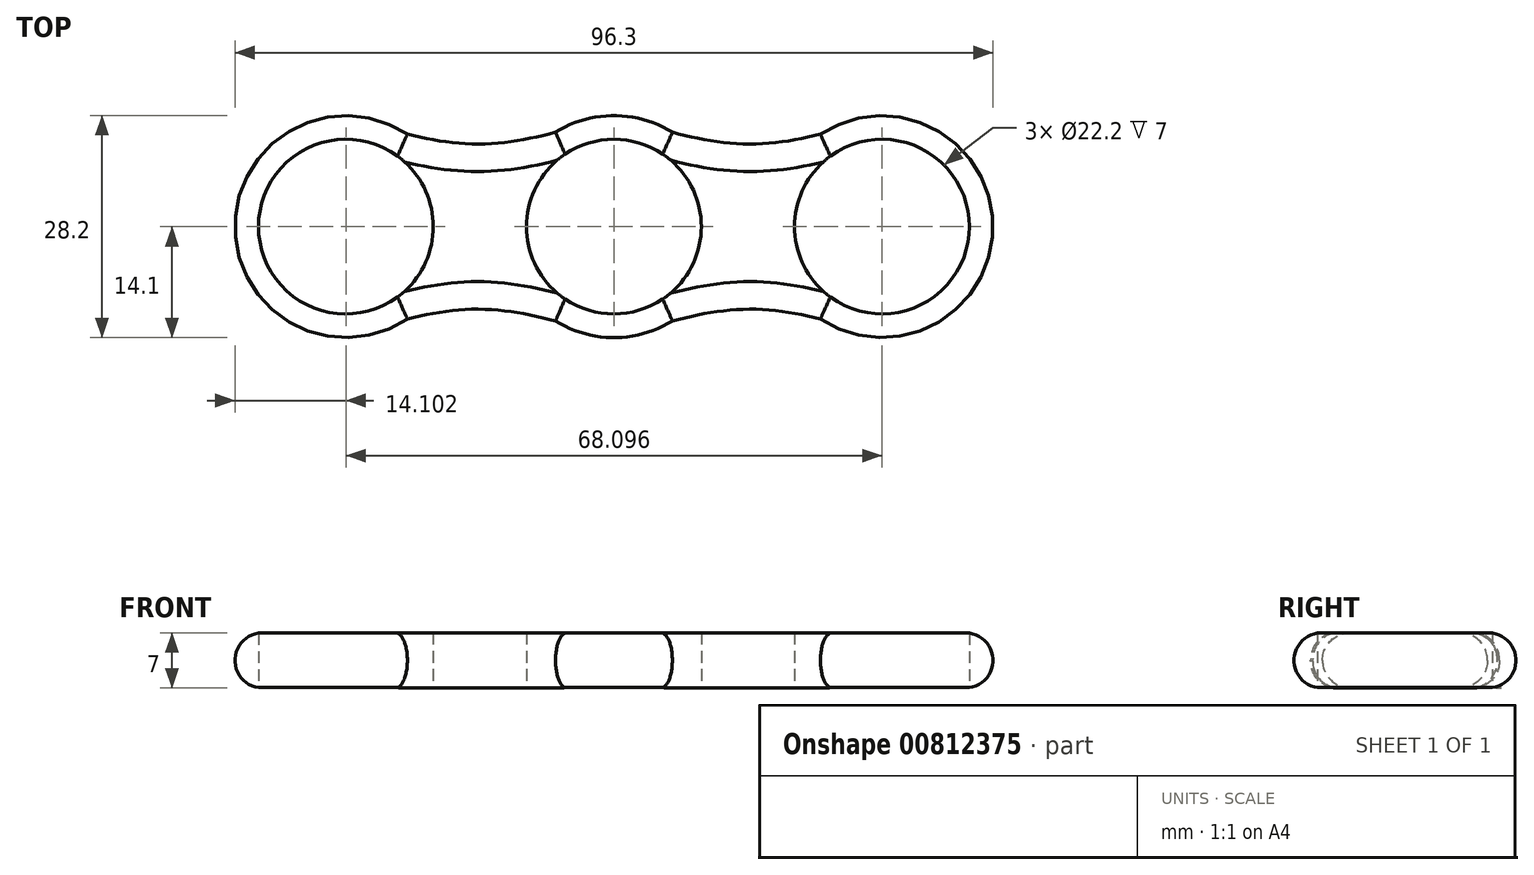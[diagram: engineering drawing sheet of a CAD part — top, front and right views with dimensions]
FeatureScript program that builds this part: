
annotation { "Feature Type Name" : "Feature", "Feature Type Description" : "" }
export const myFeature = defineFeature(function(context is Context, id is Id, definition is map)
    precondition{}
    {
        {
            var Q0;
            Q0=qCreatedBy(makeId("Top.planeOp"),FACE);
            var sketch = newSketch(context, id + "F0", { "sketchPlane" : qUnion([Q0])});
            skCircle(sketch, "E0", {"center": v(0, 0) * mm, "radius": 11.1 * mm});
            skCircle(sketch, "E1", {"center": v(0, 0) * mm, "radius": 14.1 * mm});
            skLineSegment(sketch, "E2", {"start": v(0, 0) * mm, "end": v(45, 0) * mm, "construction": true});
            skCircle(sketch, "E3", {"center": v(34.05, 0) * mm, "radius": 11.1 * mm});
            skCircle(sketch, "E4", {"center": v(34.05, 0) * mm, "radius": 14.1 * mm});
            skLineSegment(sketch, "E5", {"start": v(34.05, -14.1) * mm, "end": v(34.05, 14.1) * mm});
            skFitSpline(sketch, "E6", {"points": [v(34.05, 14.1) * mm, v(0, 14.1) * mm], "startDerivative": vector(-47.35, -16.05) * mm, "endDerivative": vector(-43.28, 12.76) * mm});
            skFitSpline(sketch, "E7.MirrorCS", {"points": [v(34.05, -14.1) * mm, v(0, -14.1) * mm], "startDerivative": vector(-47.35, 16.05) * mm, "endDerivative": vector(-43.28, -12.76) * mm});
            skLineSegment(sketch, "E8", {"start": v(0, -14.1) * mm, "end": v(0, 14.1) * mm, "construction": true});
            skFitSpline(sketch, "E9.MirrorCS", {"points": [v(-34.05, 14.1) * mm, v(0, 14.1) * mm], "startDerivative": vector(47.35, -16.05) * mm, "endDerivative": vector(43.28, 12.76) * mm});
            skCircle(sketch, "E10.MirrorC", {"center": v(-34.05, 0) * mm, "radius": 11.1 * mm});
            skCircle(sketch, "E11.MirrorC", {"center": v(-34.05, 0) * mm, "radius": 14.1 * mm});
            skFitSpline(sketch, "E12.MirrorCS", {"points": [v(-34.05, -14.1) * mm, v(0, -14.1) * mm], "startDerivative": vector(47.35, 16.05) * mm, "endDerivative": vector(43.28, -12.76) * mm});
            skSolve(sketch);
        }
        {
            var Q0;
            Q0 = qSketchRegion(id + "F0", true);
            extrude(context, id + "F1", {"entities" : qUnion([Q0]), "depth" : 7 * mm, "offsetDistance" : 25 * mm});
        }
        {
            var Q0;
            Q0=makeQuery(id+"F1.opExtrude","CAP_EDGE",EDGE,{"disambiguationData":[OSD([sQuery(id+"F0.wireOp",EDGE,"E9.MirrorCS")])],"isStart":false});
            var Q1;
            Q1=makeQuery(id+"F1.opExtrude","CAP_EDGE",EDGE,{"disambiguationData":[OSD([sQuery(id+"F0.wireOp",EDGE,"E11.MirrorC")])],"isStart":false});
            var Q2;
            Q2=makeQuery(id+"F1.opExtrude","CAP_EDGE",EDGE,{"disambiguationData":[OSD([sQuery(id+"F0.wireOp",EDGE,"E12.MirrorCS")])],"isStart":false});
            var Q3;
            {var subQ0=sQuery(id+"F0.wireOp",EDGE,"E12.MirrorCS");var subQ1=sQuery(id+"F0.wireOp",EDGE,"E7.MirrorCS");var subQ2=sQuery(id+"F0.wireOp",EDGE,"E1");Q3=makeQuery(id+"F1.opExtrude","CAP_EDGE",EDGE,{"disambiguationData":[OSD([subQ2]),TDD([makeQuery(id+"F0.imprint","IMPRINT",EDGE,{"disambiguationData":[TD([[makeQuery(id+"F0.imprint","INTERSECT",VERTEX,{"derivedFrom":[subQ2,subQ0]}),-1.0]])],"derivedFrom":subQ2}),makeQuery(id+"F0.imprint","IMPRINT",EDGE,{"disambiguationData":[TD([[makeQuery(id+"F0.imprint","INTERSECT",VERTEX,{"derivedFrom":[subQ2,subQ1]}),1.0]])],"derivedFrom":subQ2})])],"isStart":false});}
            var Q4;
            Q4=makeQuery(id+"F1.opExtrude","CAP_EDGE",EDGE,{"disambiguationData":[OSD([sQuery(id+"F0.wireOp",EDGE,"E7.MirrorCS")])],"isStart":false});
            var Q5;
            {var subQ0=sQuery(id+"F0.wireOp",EDGE,"E9.MirrorCS");var subQ1=sQuery(id+"F0.wireOp",EDGE,"E6");var subQ2=sQuery(id+"F0.wireOp",EDGE,"E1");Q5=makeQuery(id+"F1.opExtrude","CAP_EDGE",EDGE,{"disambiguationData":[OSD([subQ2]),TDD([makeQuery(id+"F0.imprint","IMPRINT",EDGE,{"disambiguationData":[TD([[makeQuery(id+"F0.imprint","INTERSECT",VERTEX,{"derivedFrom":[subQ2,subQ1]}),-1.0]])],"derivedFrom":subQ2}),makeQuery(id+"F0.imprint","IMPRINT",EDGE,{"disambiguationData":[TD([[makeQuery(id+"F0.imprint","INTERSECT",VERTEX,{"derivedFrom":[subQ2,subQ0]}),1.0]])],"derivedFrom":subQ2})])],"isStart":false});}
            var Q6;
            Q6=makeQuery(id+"F1.opExtrude","CAP_EDGE",EDGE,{"disambiguationData":[OSD([sQuery(id+"F0.wireOp",EDGE,"E6")])],"isStart":false});
            var Q7;
            Q7=makeQuery(id+"F1.opExtrude","CAP_EDGE",EDGE,{"disambiguationData":[OSD([sQuery(id+"F0.wireOp",EDGE,"E4")])],"isStart":false});
            var Q8;
            Q8=makeQuery(id+"F1.opExtrude","CAP_EDGE",EDGE,{"disambiguationData":[OSD([sQuery(id+"F0.wireOp",EDGE,"E11.MirrorC")])],"isStart":true});
            var Q9;
            Q9=makeQuery(id+"F1.opExtrude","CAP_EDGE",EDGE,{"disambiguationData":[OSD([sQuery(id+"F0.wireOp",EDGE,"E9.MirrorCS")])],"isStart":true});
            var Q10;
            Q10=makeQuery(id+"F1.opExtrude","CAP_EDGE",EDGE,{"disambiguationData":[OSD([sQuery(id+"F0.wireOp",EDGE,"E6")])],"isStart":true});
            var Q11;
            Q11=makeQuery(id+"F1.opExtrude","CAP_EDGE",EDGE,{"disambiguationData":[OSD([sQuery(id+"F0.wireOp",EDGE,"E4")])],"isStart":true});
            var Q12;
            {var subQ0=sQuery(id+"F0.wireOp",EDGE,"E9.MirrorCS");var subQ1=sQuery(id+"F0.wireOp",EDGE,"E6");var subQ2=sQuery(id+"F0.wireOp",EDGE,"E1");Q12=makeQuery(id+"F1.opExtrude","CAP_EDGE",EDGE,{"disambiguationData":[OSD([subQ2]),TDD([makeQuery(id+"F0.imprint","IMPRINT",EDGE,{"disambiguationData":[TD([[makeQuery(id+"F0.imprint","INTERSECT",VERTEX,{"derivedFrom":[subQ2,subQ1]}),-1.0]])],"derivedFrom":subQ2}),makeQuery(id+"F0.imprint","IMPRINT",EDGE,{"disambiguationData":[TD([[makeQuery(id+"F0.imprint","INTERSECT",VERTEX,{"derivedFrom":[subQ2,subQ0]}),1.0]])],"derivedFrom":subQ2})])],"isStart":true});}
            var Q13;
            Q13=makeQuery(id+"F1.opExtrude","CAP_EDGE",EDGE,{"disambiguationData":[OSD([sQuery(id+"F0.wireOp",EDGE,"E7.MirrorCS")])],"isStart":true});
            var Q14;
            {var subQ0=sQuery(id+"F0.wireOp",EDGE,"E12.MirrorCS");var subQ1=sQuery(id+"F0.wireOp",EDGE,"E7.MirrorCS");var subQ2=sQuery(id+"F0.wireOp",EDGE,"E1");Q14=makeQuery(id+"F1.opExtrude","CAP_EDGE",EDGE,{"disambiguationData":[OSD([subQ2]),TDD([makeQuery(id+"F0.imprint","IMPRINT",EDGE,{"disambiguationData":[TD([[makeQuery(id+"F0.imprint","INTERSECT",VERTEX,{"derivedFrom":[subQ2,subQ0]}),-1.0]])],"derivedFrom":subQ2}),makeQuery(id+"F0.imprint","IMPRINT",EDGE,{"disambiguationData":[TD([[makeQuery(id+"F0.imprint","INTERSECT",VERTEX,{"derivedFrom":[subQ2,subQ1]}),1.0]])],"derivedFrom":subQ2})])],"isStart":true});}
            var Q15;
            Q15=makeQuery(id+"F1.opExtrude","CAP_EDGE",EDGE,{"disambiguationData":[OSD([sQuery(id+"F0.wireOp",EDGE,"E12.MirrorCS")])],"isStart":true});
            fillet(context, id + "F2", {"entities" : qUnion([Q0, Q1, Q2, Q3, Q4, Q5, Q6, Q7, Q8, Q9, Q10, Q11, Q12, Q13, Q14, Q15]), "radius" : 3.5 * mm, "tangentPropagation" : true, "allowEdgeOverflow" : false});
        }
    });
